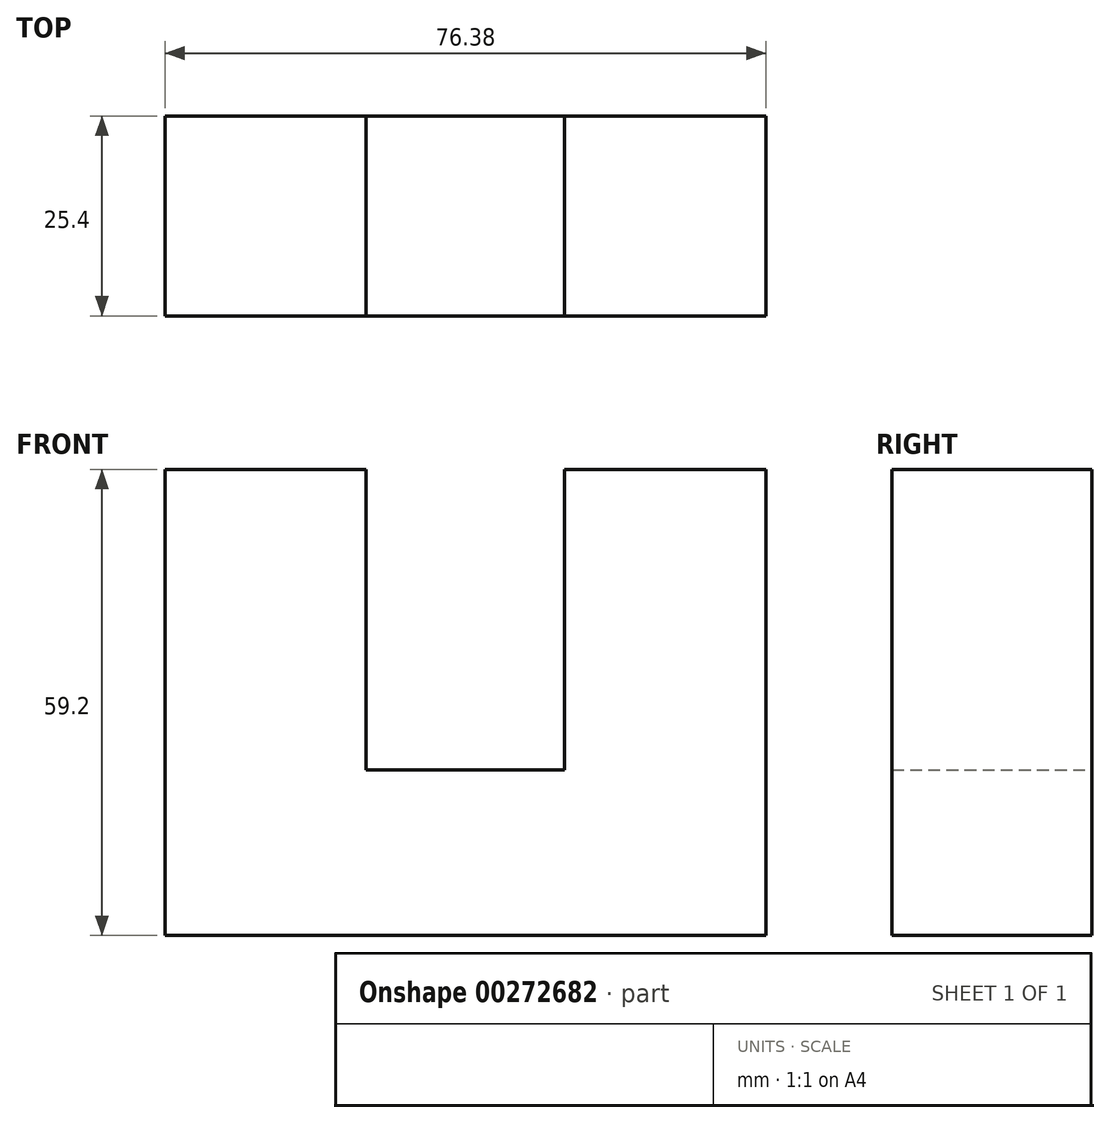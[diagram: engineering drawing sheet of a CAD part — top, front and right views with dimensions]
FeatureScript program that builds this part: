
annotation { "Feature Type Name" : "Feature", "Feature Type Description" : "" }
export const myFeature = defineFeature(function(context is Context, id is Id, definition is map)
    precondition{}
    {
        {
            var Q0;
            Q0=qCreatedBy(makeId("Front.planeOp"),FACE);
            var sketch = newSketch(context, id + "F0", { "sketchPlane" : qUnion([Q0])});
            skLineSegment(sketch, "E0", {"start": v(0, 0) * mm, "end": v(-76.38, 0) * mm});
            skLineSegment(sketch, "E1", {"start": v(-76.38, 0) * mm, "end": v(-76.38, 59.2) * mm});
            skLineSegment(sketch, "E2", {"start": v(-76.38, 59.2) * mm, "end": v(-50.8, 59.2) * mm});
            skLineSegment(sketch, "E3", {"start": v(-50.8, 59.2) * mm, "end": v(-50.8, 21) * mm});
            skLineSegment(sketch, "E4", {"start": v(-50.8, 21) * mm, "end": v(-25.59, 21) * mm});
            skLineSegment(sketch, "E5", {"start": v(-25.59, 21) * mm, "end": v(-25.59, 59.2) * mm});
            skLineSegment(sketch, "E6", {"start": v(-25.59, 59.2) * mm, "end": v(0, 59.2) * mm});
            skLineSegment(sketch, "E7", {"start": v(0, 59.2) * mm, "end": v(0, 0) * mm});
            skSolve(sketch);
        }
        {
            var Q0;
            Q0=makeQuery(id+"F0.imprint","IMPRINT",FACE,{"disambiguationData":[TD([[makeQuery(id+"F0.imprint","IMPRINT",EDGE,{"derivedFrom":sQuery(id+"F0.wireOp",EDGE,"E0")}),-1.0]])]});
            extrude(context, id + "F1", {"entities" : qUnion([Q0]), "depth" : 25.4 * mm});
        }
    });
